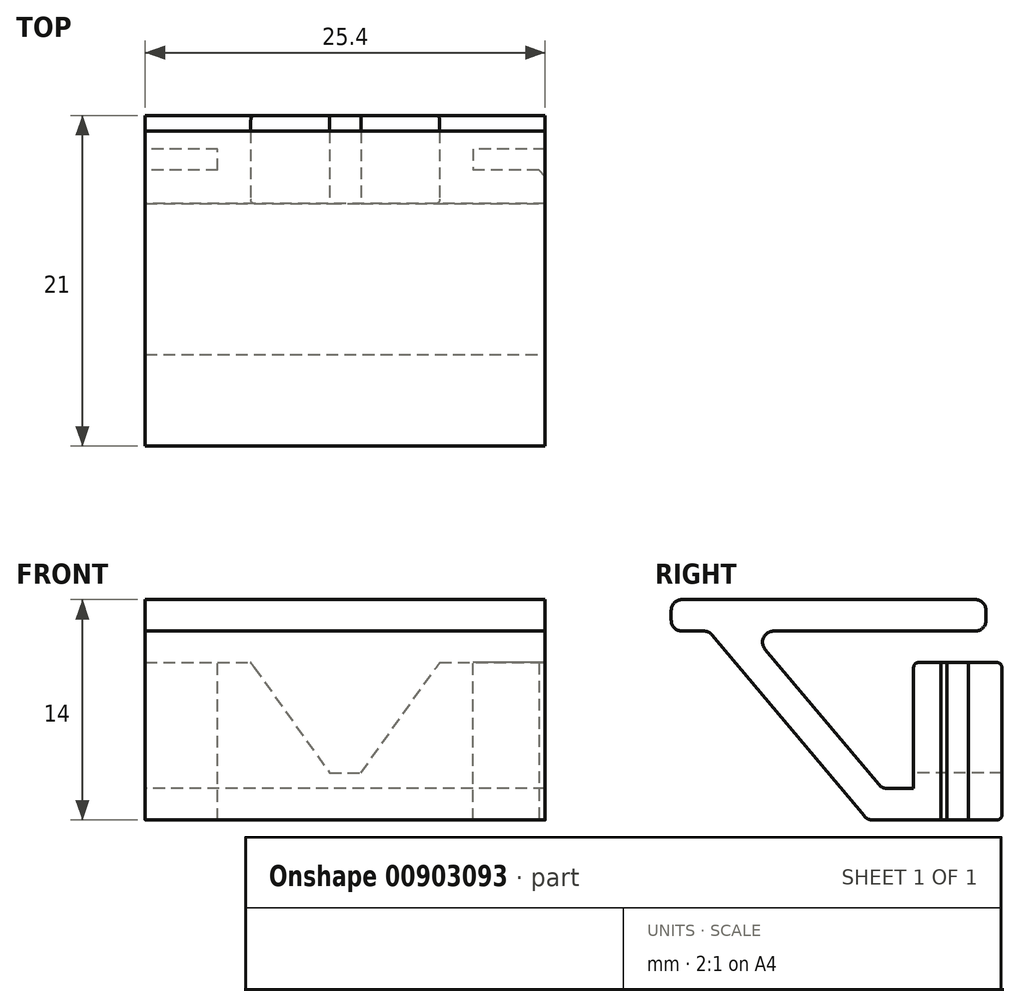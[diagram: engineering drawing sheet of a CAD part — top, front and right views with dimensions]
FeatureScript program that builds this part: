
annotation { "Feature Type Name" : "Feature", "Feature Type Description" : "" }
export const myFeature = defineFeature(function(context is Context, id is Id, definition is map)
    precondition{}
    {
        {
            var Q0;
            Q0=qCreatedBy(makeId("Top.planeOp"),FACE);
            var sketch = newSketch(context, id + "F0", { "sketchPlane" : qUnion([Q0])});
            skLineSegment(sketch, "E0.bottom", {"start": v(-12.7, -2.8) * mm, "end": v(12.7, -2.8) * mm});
            skLineSegment(sketch, "E0.top", {"start": v(-12.7, 2.8) * mm, "end": v(12.7, 2.8) * mm});
            skLineSegment(sketch, "E0.left", {"start": v(-12.7, 2.8) * mm, "end": v(-12.7, -2.8) * mm});
            skLineSegment(sketch, "E0.right", {"start": v(12.7, 2.8) * mm, "end": v(12.7, -2.8) * mm});
            skLineSegment(sketch, "E1", {"start": v(0, 2.8) * mm, "end": v(0, -2.8) * mm, "construction": true});
            skSolve(sketch);
        }
        {
            var Q0;
            Q0=makeQuery(id+"F0.imprint","IMPRINT",FACE,{"disambiguationData":[TD([[makeQuery(id+"F0.imprint","IMPRINT",EDGE,{"derivedFrom":sQuery(id+"F0.wireOp",EDGE,"E0.bottom")}),1.0]])]});
            extrude(context, id + "F1", {"entities" : qUnion([Q0]), "depth" : 10 * mm, "offsetDistance" : 25 * mm});
        }
        {
            var Q0;
            Q0=makeQuery(id+"F1.opExtrude","CAP_FACE",FACE,{"disambiguationData":[OSD([sQuery(id+"F0.wireOp",EDGE,"E0.bottom"),sQuery(id+"F0.wireOp",EDGE,"E0.top"),sQuery(id+"F0.wireOp",EDGE,"E0.left"),sQuery(id+"F0.wireOp",EDGE,"E0.right")])],"isStart":false});
            var sketch = newSketch(context, id + "F2", { "sketchPlane" : qUnion([Q0])});
            skLineSegment(sketch, "E2.bottom", {"start": v(-12.7, -0.68) * mm, "end": v(-8.1, -0.68) * mm});
            skLineSegment(sketch, "E2.top", {"start": v(-12.7, 0.67) * mm, "end": v(-8.1, 0.67) * mm});
            skLineSegment(sketch, "E2.left", {"start": v(-12.7, 0.68) * mm, "end": v(-12.7, -0.68) * mm});
            skLineSegment(sketch, "E2.right", {"start": v(-8.1, 0.68) * mm, "end": v(-8.1, -0.68) * mm});
            skLineSegment(sketch, "E3", {"start": v(-12.7, 0) * mm, "end": v(-8.1, 0) * mm, "construction": true});
            skLineSegment(sketch, "E4.MirrorCS", {"start": v(12.7, 0.68) * mm, "end": v(8.1, 0.67) * mm});
            skLineSegment(sketch, "E5.MirrorCS", {"start": v(8.1, 0.68) * mm, "end": v(8.1, -0.68) * mm});
            skLineSegment(sketch, "E6.MirrorCS", {"start": v(12.7, -0.67) * mm, "end": v(8.1, -0.67) * mm});
            skLineSegment(sketch, "E7.MirrorCS", {"start": v(12.7, 0.68) * mm, "end": v(12.7, -0.68) * mm});
            skSolve(sketch);
        }
        {
            var Q0;
            Q0=makeQuery(id+"F2.imprint","IMPRINT",FACE,{"disambiguationData":[TD([[makeQuery(id+"F2.imprint","IMPRINT",EDGE,{"derivedFrom":sQuery(id+"F2.wireOp",EDGE,"E2.bottom")}),1.0]])]});
            var Q1;
            Q1=makeQuery(id+"F2.imprint","IMPRINT",FACE,{"disambiguationData":[TD([[makeQuery(id+"F2.imprint","IMPRINT",EDGE,{"derivedFrom":sQuery(id+"F2.wireOp",EDGE,"E4.MirrorCS")}),1.0]])]});
            extrude(context, id + "F3", {"entities" : qUnion([Q0, Q1]), "operationType" : NewBodyOperationType.REMOVE, "endBound" : BoundingType.UP_TO_NEXT, "oppositeDirection" : true, "depth" : 25 * mm, "offsetDistance" : 25 * mm});
        }
        {
            var Q0;
            Q0=makeQuery(id+"F1.opExtrude","SWEPT_FACE",FACE,{"disambiguationData":[OSD([sQuery(id+"F0.wireOp",EDGE,"E0.bottom")])]});
            var sketch = newSketch(context, id + "F4", { "sketchPlane" : qUnion([Q0])});
            skLineSegment(sketch, "E8", {"start": v(-6, 10) * mm, "end": v(-1, 3) * mm});
            skLineSegment(sketch, "E9", {"start": v(-1, 3) * mm, "end": v(1, 3) * mm});
            skLineSegment(sketch, "E10", {"start": v(1, 3) * mm, "end": v(6, 10) * mm});
            skLineSegment(sketch, "E11", {"start": v(6, 10) * mm, "end": v(-6, 10) * mm});
            skLineSegment(sketch, "E12", {"start": v(0, 10) * mm, "end": v(0, 3) * mm, "construction": true});
            skSolve(sketch);
        }
        {
            var Q0;
            Q0=makeQuery(id+"F4.imprint","IMPRINT",FACE,{"disambiguationData":[TD([[makeQuery(id+"F4.imprint","IMPRINT",EDGE,{"derivedFrom":sQuery(id+"F4.wireOp",EDGE,"E8")}),1.0]])]});
            extrude(context, id + "F5", {"entities" : qUnion([Q0]), "operationType" : NewBodyOperationType.REMOVE, "endBound" : BoundingType.UP_TO_NEXT, "oppositeDirection" : true, "depth" : 25 * mm, "offsetDistance" : 25 * mm});
        }
        {
            var Q0;
            {var subQ0=sQuery(id+"F0.wireOp",EDGE,"E0.bottom");var subQ2=sQuery(id+"F0.wireOp",EDGE,"E0.left");Q0=makeQuery(id+"F3.boolean.opBoolean","SPLIT",FACE,{"disambiguationData":[TD([makeQuery(id+"F1.opExtrude","SWEPT_FACE",FACE,{"disambiguationData":[OSD([subQ0])]})])],"derivedFrom":makeQuery(id+"F1.opExtrude","SWEPT_FACE",FACE,{"disambiguationData":[OSD([subQ2])]})});}
            var sketch = newSketch(context, id + "F6", { "sketchPlane" : qUnion([Q0])});
            skLineSegment(sketch, "E13", {"start": v(2.8, 0) * mm, "end": v(5.73, 0) * mm});
            skLineSegment(sketch, "E14", {"start": v(5.73, 0) * mm, "end": v(15.81, 12) * mm});
            skLineSegment(sketch, "E15", {"start": v(15.81, 12) * mm, "end": v(18.2, 12) * mm});
            skLineSegment(sketch, "E16", {"start": v(18.2, 12) * mm, "end": v(18.2, 14) * mm});
            skLineSegment(sketch, "E17", {"start": v(18.2, 14) * mm, "end": v(-1.8, 14) * mm});
            skLineSegment(sketch, "E18", {"start": v(-1.8, 14) * mm, "end": v(-1.8, 12) * mm});
            skLineSegment(sketch, "E19", {"start": v(-1.8, 12) * mm, "end": v(13.2, 12) * mm});
            skLineSegment(sketch, "E20", {"start": v(13.2, 12) * mm, "end": v(4.8, 2) * mm});
            skLineSegment(sketch, "E21", {"start": v(4.8, 2) * mm, "end": v(2.8, 2) * mm});
            skLineSegment(sketch, "E22", {"start": v(2.8, 2) * mm, "end": v(2.8, 0) * mm});
            skSolve(sketch);
        }
        {
            var Q0;
            Q0=makeQuery(id+"F6.imprint","IMPRINT",FACE,{"disambiguationData":[TD([[makeQuery(id+"F6.imprint","IMPRINT",EDGE,{"derivedFrom":sQuery(id+"F6.wireOp",EDGE,"E13")}),1.0]])]});
            var Q1;
            {var subQ0=sQuery(id+"F0.wireOp",EDGE,"E0.bottom");var subQ1=sQuery(id+"F0.wireOp",EDGE,"E0.right");Q1=makeQuery(id+"F3.boolean.opBoolean","SPLIT",FACE,{"disambiguationData":[TD([makeQuery(id+"F1.opExtrude","SWEPT_FACE",FACE,{"disambiguationData":[OSD([subQ0])]})])],"derivedFrom":makeQuery(id+"F1.opExtrude","SWEPT_FACE",FACE,{"disambiguationData":[OSD([subQ1])]})});}
            extrude(context, id + "F7", {"entities" : qUnion([Q0]), "operationType" : NewBodyOperationType.ADD, "endBound" : BoundingType.UP_TO_SURFACE, "oppositeDirection" : true, "depth" : 25 * mm, "endBoundEntityFace" : qUnion([Q1]), "offsetDistance" : 25 * mm});
        }
        {
            var Q0;
            Q0=makeQuery(id+"F3.boolean.opBoolean","COPY",EDGE,{"derivedFrom":makeQuery(id+"F3.opExtrude","SWEPT_EDGE",EDGE,{"disambiguationData":[OSD([sQuery(id+"F0.wireOp",EDGE,"E0.right"),sQuery(id+"F2.wireOp",EDGE,"E4.MirrorCS"),sQuery(id+"F2.wireOp",EDGE,"E7.MirrorCS")])]})});
            var Q1;
            Q1=makeQuery(id+"F3.boolean.opBoolean","COPY",EDGE,{"derivedFrom":makeQuery(id+"F3.opExtrude","SWEPT_EDGE",EDGE,{"disambiguationData":[OSD([sQuery(id+"F0.wireOp",EDGE,"E0.right"),sQuery(id+"F2.wireOp",EDGE,"E6.MirrorCS"),sQuery(id+"F2.wireOp",EDGE,"E7.MirrorCS")])]})});
            chamfer(context, id + "F8", {"entities" : qUnion([Q0, Q1]), "width" : 0.4 * mm, "tangentPropagation" : true});
        }
        {
            var Q0;
            Q0=makeQuery(id+"F7.opExtrude","SWEPT_EDGE",EDGE,{"disambiguationData":[OSD([sQuery(id+"F0.wireOp",EDGE,"E0.bottom"),sQuery(id+"F0.wireOp",EDGE,"E0.left"),sQuery(id+"F6.wireOp",EDGE,"E21"),sQuery(id+"F6.wireOp",EDGE,"E22")])]});
            var Q1;
            Q1=makeQuery(id+"F7.opExtrude","SWEPT_EDGE",EDGE,{"disambiguationData":[OSD([sQuery(id+"F6.wireOp",EDGE,"E20"),sQuery(id+"F6.wireOp",EDGE,"E21")])]});
            var Q2;
            Q2=makeQuery(id+"F7.opExtrude","SWEPT_EDGE",EDGE,{"disambiguationData":[OSD([sQuery(id+"F6.wireOp",EDGE,"E19"),sQuery(id+"F6.wireOp",EDGE,"E20")])]});
            var Q3;
            Q3=makeQuery(id+"F7.opExtrude","SWEPT_EDGE",EDGE,{"disambiguationData":[OSD([sQuery(id+"F6.wireOp",EDGE,"E14"),sQuery(id+"F6.wireOp",EDGE,"E15")])]});
            var Q4;
            Q4=makeQuery(id+"F7.opExtrude","SWEPT_EDGE",EDGE,{"disambiguationData":[OSD([sQuery(id+"F6.wireOp",EDGE,"E13"),sQuery(id+"F6.wireOp",EDGE,"E14")])]});
            var Q5;
            Q5=makeQuery(id+"F7.opExtrude","SWEPT_EDGE",EDGE,{"disambiguationData":[OSD([sQuery(id+"F6.wireOp",EDGE,"E15"),sQuery(id+"F6.wireOp",EDGE,"E16")])]});
            var Q6;
            Q6=makeQuery(id+"F7.opExtrude","SWEPT_EDGE",EDGE,{"disambiguationData":[OSD([sQuery(id+"F6.wireOp",EDGE,"E16"),sQuery(id+"F6.wireOp",EDGE,"E17")])]});
            var Q7;
            Q7=makeQuery(id+"F7.opExtrude","SWEPT_EDGE",EDGE,{"disambiguationData":[OSD([sQuery(id+"F6.wireOp",EDGE,"E18"),sQuery(id+"F6.wireOp",EDGE,"E19")])]});
            var Q8;
            Q8=makeQuery(id+"F7.opExtrude","SWEPT_EDGE",EDGE,{"disambiguationData":[OSD([sQuery(id+"F6.wireOp",EDGE,"E17"),sQuery(id+"F6.wireOp",EDGE,"E18")])]});
            fillet(context, id + "F9", {"entities" : qUnion([Q0, Q1, Q2, Q3, Q4, Q5, Q6, Q7, Q8]), "radius" : 0.7 * mm, "tangentPropagation" : true, "allowEdgeOverflow" : false});
        }
        {
            var Q0;
            Q0=makeQuery(id+"F1.opExtrude","CAP_EDGE",EDGE,{"disambiguationData":[OSD([sQuery(id+"F0.wireOp",EDGE,"E0.top")])],"isStart":true});
            var Q1;
            {var subQ0=sQuery(id+"F0.wireOp",EDGE,"E0.right");var subQ1=sQuery(id+"F0.wireOp",EDGE,"E0.top");Q1=makeQuery(id+"F5.boolean.opBoolean","SPLIT",EDGE,{"disambiguationData":[TD([makeQuery(id+"F1.opExtrude","SWEPT_FACE",FACE,{"disambiguationData":[OSD([subQ0])]})])],"derivedFrom":makeQuery(id+"F1.opExtrude","CAP_EDGE",EDGE,{"disambiguationData":[OSD([subQ1])],"isStart":false})});}
            var Q2;
            {var subQ0=sQuery(id+"F0.wireOp",EDGE,"E0.left");var subQ1=sQuery(id+"F0.wireOp",EDGE,"E0.top");Q2=makeQuery(id+"F5.boolean.opBoolean","SPLIT",EDGE,{"disambiguationData":[TD([makeQuery(id+"F1.opExtrude","SWEPT_FACE",FACE,{"disambiguationData":[OSD([subQ0])]})])],"derivedFrom":makeQuery(id+"F1.opExtrude","CAP_EDGE",EDGE,{"disambiguationData":[OSD([subQ1])],"isStart":false})});}
            var Q3;
            Q3=makeQuery(id+"F3.boolean.opBoolean","COPY",EDGE,{"derivedFrom":makeQuery(id+"F3.opExtrude","CAP_EDGE",EDGE,{"disambiguationData":[OSD([sQuery(id+"F2.wireOp",EDGE,"E2.top")])],"isStart":false})});
            var Q4;
            Q4=makeQuery(id+"F3.boolean.opBoolean","COPY",EDGE,{"derivedFrom":makeQuery(id+"F3.opExtrude","CAP_EDGE",EDGE,{"disambiguationData":[OSD([sQuery(id+"F2.wireOp",EDGE,"E4.MirrorCS")])],"isStart":false})});
            var Q5;
            Q5=makeQuery(id+"F3.boolean.opBoolean","COPY",EDGE,{"derivedFrom":makeQuery(id+"F3.opExtrude","CAP_EDGE",EDGE,{"disambiguationData":[OSD([sQuery(id+"F2.wireOp",EDGE,"E6.MirrorCS")])],"isStart":false})});
            var Q6;
            Q6=makeQuery(id+"F3.boolean.opBoolean","COPY",EDGE,{"derivedFrom":makeQuery(id+"F3.opExtrude","CAP_EDGE",EDGE,{"disambiguationData":[OSD([sQuery(id+"F2.wireOp",EDGE,"E2.bottom")])],"isStart":false})});
            var Q7;
            Q7=makeQuery(id+"F3.boolean.opBoolean","COPY",EDGE,{"derivedFrom":makeQuery(id+"F3.opExtrude","CAP_EDGE",EDGE,{"disambiguationData":[OSD([sQuery(id+"F2.wireOp",EDGE,"E4.MirrorCS")])],"isStart":true})});
            var Q8;
            Q8=makeQuery(id+"F3.boolean.opBoolean","COPY",EDGE,{"derivedFrom":makeQuery(id+"F3.opExtrude","CAP_EDGE",EDGE,{"disambiguationData":[OSD([sQuery(id+"F2.wireOp",EDGE,"E6.MirrorCS")])],"isStart":true})});
            var Q9;
            {var subQ0=sQuery(id+"F0.wireOp",EDGE,"E0.bottom");var subQ1=sQuery(id+"F0.wireOp",EDGE,"E0.right");Q9=makeQuery(id+"F5.boolean.opBoolean","SPLIT",EDGE,{"disambiguationData":[TD([makeQuery(id+"F1.opExtrude","SWEPT_FACE",FACE,{"disambiguationData":[OSD([subQ1])]})])],"derivedFrom":makeQuery(id+"F1.opExtrude","CAP_EDGE",EDGE,{"disambiguationData":[OSD([subQ0])],"isStart":false})});}
            var Q10;
            Q10=makeQuery(id+"F3.boolean.opBoolean","COPY",EDGE,{"derivedFrom":makeQuery(id+"F3.opExtrude","CAP_EDGE",EDGE,{"disambiguationData":[OSD([sQuery(id+"F2.wireOp",EDGE,"E2.top")])],"isStart":true})});
            var Q11;
            Q11=makeQuery(id+"F3.boolean.opBoolean","COPY",EDGE,{"derivedFrom":makeQuery(id+"F3.opExtrude","CAP_EDGE",EDGE,{"disambiguationData":[OSD([sQuery(id+"F2.wireOp",EDGE,"E2.bottom")])],"isStart":true})});
            var Q12;
            {var subQ0=sQuery(id+"F0.wireOp",EDGE,"E0.bottom");var subQ1=sQuery(id+"F0.wireOp",EDGE,"E0.left");Q12=makeQuery(id+"F5.boolean.opBoolean","SPLIT",EDGE,{"disambiguationData":[TD([makeQuery(id+"F1.opExtrude","SWEPT_FACE",FACE,{"disambiguationData":[OSD([subQ1])]})])],"derivedFrom":makeQuery(id+"F1.opExtrude","CAP_EDGE",EDGE,{"disambiguationData":[OSD([subQ0])],"isStart":false})});}
            var Q13;
            Q13=makeQuery(id+"F5.boolean.opBoolean","COPY",EDGE,{"derivedFrom":makeQuery(id+"F5.opExtrude","CAP_EDGE",EDGE,{"disambiguationData":[OSD([sQuery(id+"F4.wireOp",EDGE,"E10")])],"isStart":false})});
            var Q14;
            Q14=makeQuery(id+"F5.boolean.opBoolean","COPY",EDGE,{"derivedFrom":makeQuery(id+"F5.opExtrude","CAP_EDGE",EDGE,{"disambiguationData":[OSD([sQuery(id+"F4.wireOp",EDGE,"E9")])],"isStart":false})});
            var Q15;
            Q15=makeQuery(id+"F5.boolean.opBoolean","COPY",EDGE,{"derivedFrom":makeQuery(id+"F5.opExtrude","CAP_EDGE",EDGE,{"disambiguationData":[OSD([sQuery(id+"F4.wireOp",EDGE,"E8")])],"isStart":false})});
            var Q16;
            Q16=makeQuery(id+"F5.boolean.opBoolean","COPY",EDGE,{"derivedFrom":makeQuery(id+"F5.opExtrude","CAP_EDGE",EDGE,{"disambiguationData":[OSD([sQuery(id+"F4.wireOp",EDGE,"E9")])],"isStart":true})});
            var Q17;
            Q17=makeQuery(id+"F5.boolean.opBoolean","COPY",EDGE,{"derivedFrom":makeQuery(id+"F5.opExtrude","CAP_EDGE",EDGE,{"disambiguationData":[OSD([sQuery(id+"F4.wireOp",EDGE,"E10")])],"isStart":true})});
            var Q18;
            Q18=makeQuery(id+"F5.boolean.opBoolean","COPY",EDGE,{"derivedFrom":makeQuery(id+"F5.opExtrude","CAP_EDGE",EDGE,{"disambiguationData":[OSD([sQuery(id+"F4.wireOp",EDGE,"E8")])],"isStart":true})});
            fillet(context, id + "F10", {"entities" : qUnion([Q0, Q1, Q2, Q3, Q4, Q5, Q6, Q7, Q8, Q9, Q10, Q11, Q12, Q13, Q14, Q15, Q16, Q17, Q18]), "radius" : 0.3 * mm, "tangentPropagation" : true, "allowEdgeOverflow" : false});
        }
    });
